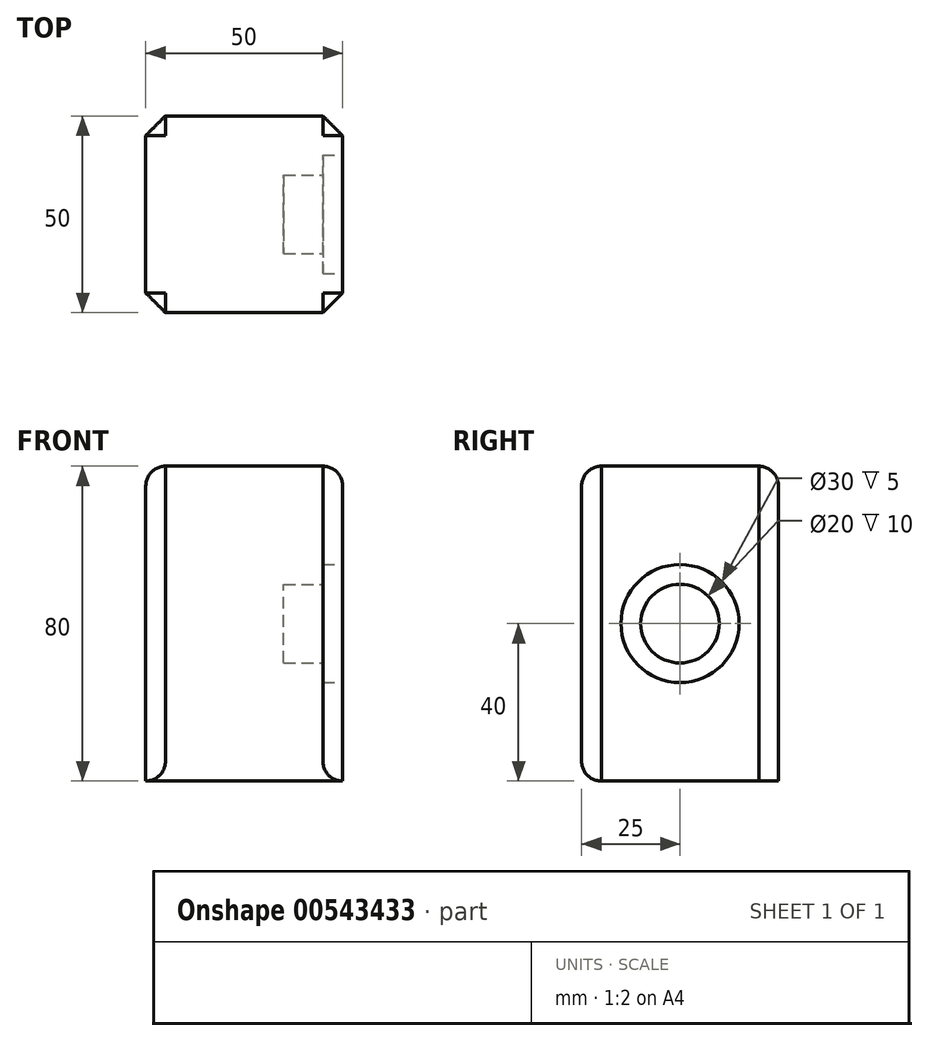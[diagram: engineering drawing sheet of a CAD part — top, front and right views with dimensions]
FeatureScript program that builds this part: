
annotation { "Feature Type Name" : "Feature", "Feature Type Description" : "" }
export const myFeature = defineFeature(function(context is Context, id is Id, definition is map)
    precondition{}
    {
        {
            var Q0;
            Q0=qCreatedBy(makeId("Top.planeOp"),FACE);
            var sketch = newSketch(context, id + "F0", { "sketchPlane" : qUnion([Q0])});
            skLineSegment(sketch, "E0.bottom", {"start": v(25, 25) * mm, "end": v(-25, 25) * mm});
            skLineSegment(sketch, "E0.top", {"start": v(25, -25) * mm, "end": v(-25, -25) * mm});
            skLineSegment(sketch, "E0.left", {"start": v(25, 25) * mm, "end": v(25, -25) * mm});
            skLineSegment(sketch, "E0.right", {"start": v(-25, 25) * mm, "end": v(-25, -25) * mm});
            skPoint(sketch, "E0.middle", {"position": v(0, 0) * mm});
            skSolve(sketch);
        }
        {
            var Q0;
            Q0=makeQuery(id+"F0.imprint","IMPRINT",FACE,{"disambiguationData":[TD([[makeQuery(id+"F0.imprint","IMPRINT",EDGE,{"derivedFrom":sQuery(id+"F0.wireOp",EDGE,"E0.bottom")}),1.0]])]});
            extrude(context, id + "F1", {"entities" : qUnion([Q0]), "endBound" : BoundingType.SYMMETRIC, "oppositeDirection" : true, "depth" : 80 * mm, "offsetDistance" : 25 * mm});
        }
        {
            var Q0;
            Q0=makeQuery(id+"F1.opExtrude","SWEPT_FACE",FACE,{"disambiguationData":[OSD([sQuery(id+"F0.wireOp",EDGE,"E0.left")])]});
            var sketch = newSketch(context, id + "F2", { "sketchPlane" : qUnion([Q0])});
            skCircle(sketch, "E1", {"center": v(0, 0) * mm, "radius": 15 * mm});
            skSolve(sketch);
        }
        {
            var Q0;
            Q0 = qSketchRegion(id + "F2", true);
            extrude(context, id + "F3", {"entities" : qUnion([Q0]), "operationType" : NewBodyOperationType.REMOVE, "oppositeDirection" : true, "depth" : 5 * mm, "offsetDistance" : 25 * mm});
        }
        {
            var Q0;
            Q0=makeQuery(id+"F3.boolean.opBoolean","COPY",FACE,{"derivedFrom":makeQuery(id+"F3.opExtrude","CAP_FACE",FACE,{"disambiguationData":[OSD([sQuery(id+"F2.wireOp",EDGE,"E1")])],"isStart":false})});
            var sketch = newSketch(context, id + "F4", { "sketchPlane" : qUnion([Q0])});
            skCircle(sketch, "E2", {"center": v(0, 0) * mm, "radius": 10 * mm});
            skSolve(sketch);
        }
        {
            var Q0;
            Q0 = qSketchRegion(id + "F4", true);
            extrude(context, id + "F5", {"entities" : qUnion([Q0]), "operationType" : NewBodyOperationType.REMOVE, "oppositeDirection" : true, "depth" : 10 * mm, "offsetDistance" : 25 * mm});
        }
        {
            var Q0;
            Q0=makeQuery(id+"F1.opExtrude","CAP_EDGE",EDGE,{"disambiguationData":[OSD([sQuery(id+"F0.wireOp",EDGE,"E0.top")])],"isStart":true});
            var Q1;
            Q1=makeQuery(id+"F1.opExtrude","CAP_EDGE",EDGE,{"disambiguationData":[OSD([sQuery(id+"F0.wireOp",EDGE,"E0.left")])],"isStart":true});
            var Q2;
            Q2=makeQuery(id+"F1.opExtrude","CAP_EDGE",EDGE,{"disambiguationData":[OSD([sQuery(id+"F0.wireOp",EDGE,"E0.bottom")])],"isStart":true});
            var Q3;
            Q3=makeQuery(id+"F1.opExtrude","CAP_EDGE",EDGE,{"disambiguationData":[OSD([sQuery(id+"F0.wireOp",EDGE,"E0.right")])],"isStart":true});
            fillet(context, id + "F6", {"entities" : qUnion([Q0, Q1, Q2, Q3]), "radius" : 5 * mm, "tangentPropagation" : true, "allowEdgeOverflow" : false});
        }
        {
            var Q0;
            Q0=makeQuery(id+"F1.opExtrude","SWEPT_EDGE",EDGE,{"disambiguationData":[OSD([sQuery(id+"F0.wireOp",EDGE,"E0.bottom"),sQuery(id+"F0.wireOp",EDGE,"E0.left")])]});
            var Q1;
            Q1=makeQuery(id+"F1.opExtrude","SWEPT_EDGE",EDGE,{"disambiguationData":[OSD([sQuery(id+"F0.wireOp",EDGE,"E0.bottom"),sQuery(id+"F0.wireOp",EDGE,"E0.right")])]});
            var Q2;
            Q2=makeQuery(id+"F1.opExtrude","SWEPT_EDGE",EDGE,{"disambiguationData":[OSD([sQuery(id+"F0.wireOp",EDGE,"E0.top"),sQuery(id+"F0.wireOp",EDGE,"E0.left")])]});
            var Q3;
            Q3=makeQuery(id+"F1.opExtrude","SWEPT_EDGE",EDGE,{"disambiguationData":[OSD([sQuery(id+"F0.wireOp",EDGE,"E0.top"),sQuery(id+"F0.wireOp",EDGE,"E0.right")])]});
            chamfer(context, id + "F7", {"entities" : qUnion([Q0, Q1, Q2, Q3]), "width" : 5 * mm, "tangentPropagation" : true});
        }
        {
            var Q0;
            Q0=makeQuery(id+"F1.opExtrude","CAP_EDGE",EDGE,{"disambiguationData":[OSD([sQuery(id+"F0.wireOp",EDGE,"E0.top")])],"isStart":false});
            fillet(context, id + "F8", {"entities" : qUnion([Q0]), "radius" : 5 * mm, "tangentPropagation" : true, "allowEdgeOverflow" : false});
        }
    });
